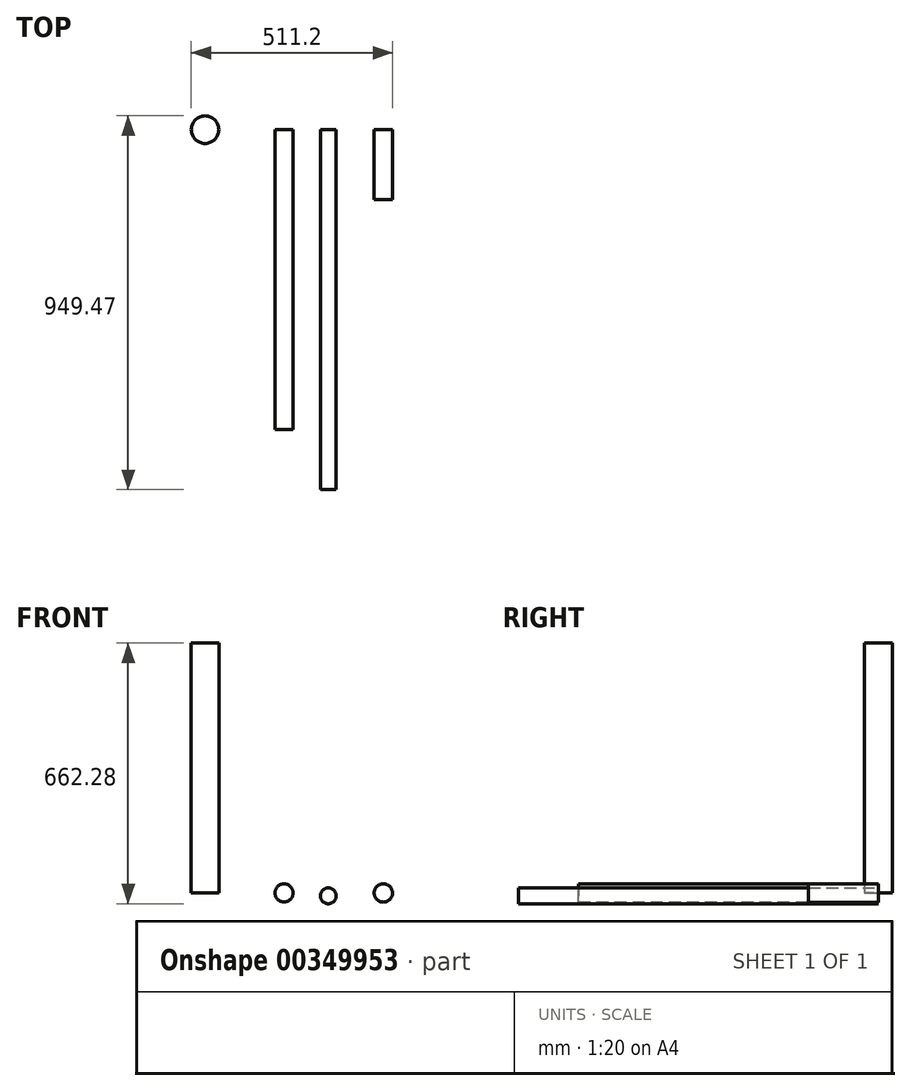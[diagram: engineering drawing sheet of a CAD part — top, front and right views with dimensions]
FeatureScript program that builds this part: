
annotation { "Feature Type Name" : "Feature", "Feature Type Description" : "" }
export const myFeature = defineFeature(function(context is Context, id is Id, definition is map)
    precondition{}
    {
        {
            var Q0;
            Q0=qCreatedBy(makeId("Front.planeOp"),FACE);
            var sketch = newSketch(context, id + "F0", { "sketchPlane" : qUnion([Q0])});
            skCircle(sketch, "E0", {"center": v(0, 0) * mm, "radius": 22.91 * mm});
            skSolve(sketch);
        }
        {
            var Q0;
            Q0 = qSketchRegion(id + "F0", true);
            extrude(context, id + "F1", {"entities" : qUnion([Q0]), "depth" : 762 * mm, "offsetDistance" : 25.4 * mm});
        }
        {
            var Q0;
            Q0=qCreatedBy(makeId("Front.planeOp"),FACE);
            var sketch = newSketch(context, id + "F2", { "sketchPlane" : qUnion([Q0])});
            skCircle(sketch, "E1", {"center": v(112.5, -7.22) * mm, "radius": 20.07 * mm});
            skSolve(sketch);
        }
        {
            var Q0;
            Q0 = qSketchRegion(id + "F2", true);
            extrude(context, id + "F3", {"entities" : qUnion([Q0]), "depth" : 914.4 * mm, "offsetDistance" : 25.4 * mm});
        }
        {
            var Q0;
            Q0=qCreatedBy(makeId("Top.planeOp"),FACE);
            var sketch = newSketch(context, id + "F4", { "sketchPlane" : qUnion([Q0])});
            skCircle(sketch, "E2", {"center": v(-200.57, 0) * mm, "radius": 35.07 * mm});
            skSolve(sketch);
        }
        {
            var Q0;
            Q0 = qSketchRegion(id + "F4", true);
            extrude(context, id + "F5", {"entities" : qUnion([Q0]), "depth" : 635 * mm, "offsetDistance" : 25.4 * mm});
        }
        {
            var Q0;
            Q0=qCreatedBy(makeId("Front.planeOp"),FACE);
            var sketch = newSketch(context, id + "F6", { "sketchPlane" : qUnion([Q0])});
            skCircle(sketch, "E3", {"center": v(252.22, 0) * mm, "radius": 23.35 * mm});
            skSolve(sketch);
        }
        {
            var Q0;
            Q0 = qSketchRegion(id + "F6", true);
            extrude(context, id + "F7", {"entities" : qUnion([Q0]), "depth" : 177.8 * mm, "offsetDistance" : 25.4 * mm});
        }
    });
